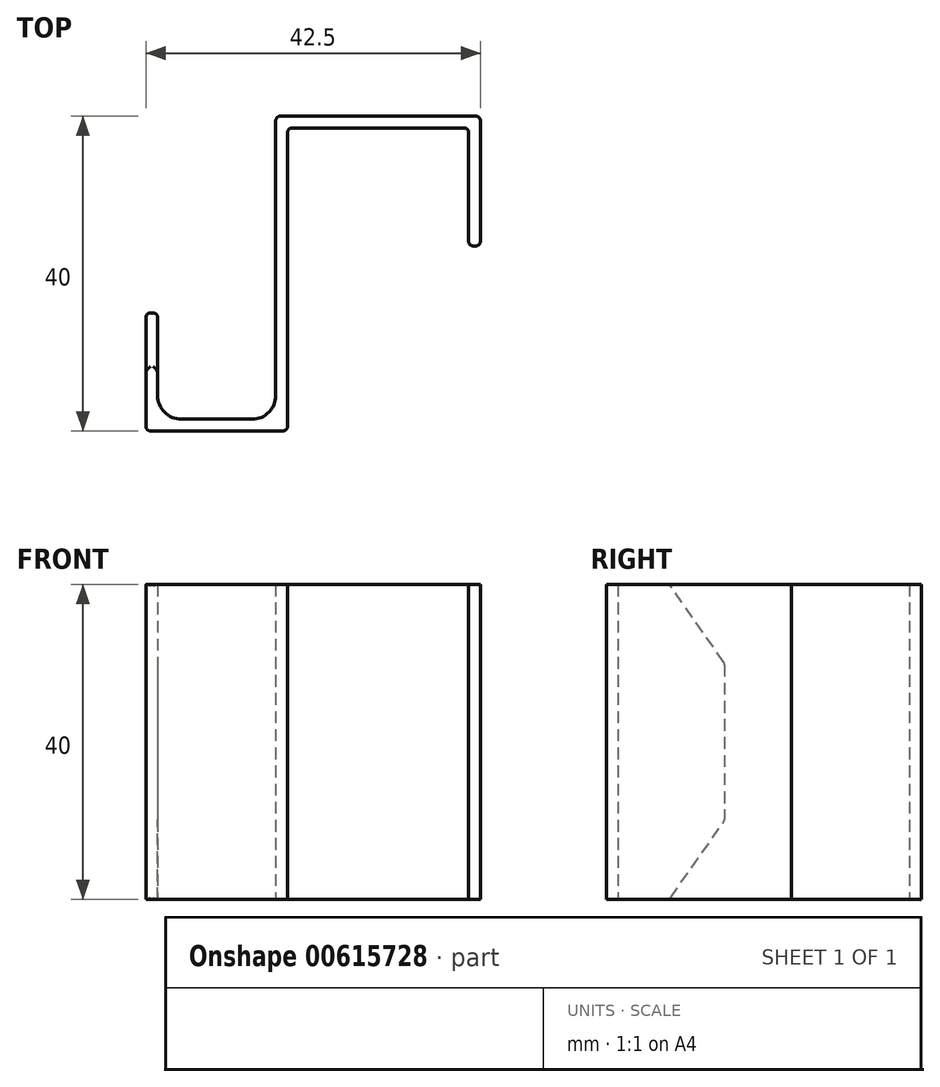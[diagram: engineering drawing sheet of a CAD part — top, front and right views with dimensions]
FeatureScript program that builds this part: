
annotation { "Feature Type Name" : "Feature", "Feature Type Description" : "" }
export const myFeature = defineFeature(function(context is Context, id is Id, definition is map)
    precondition{}
    {
        {
            var Q0;
            Q0=qCreatedBy(makeId("Top.planeOp"),FACE);
            var sketch = newSketch(context, id + "F0", { "sketchPlane" : qUnion([Q0])});
            skLineSegment(sketch, "E0.bottom", {"start": v(9.7, 5.03) * mm, "end": v(32.7, 5.03) * mm});
            skLineSegment(sketch, "E0.left", {"start": v(9.7, 5.03) * mm, "end": v(9.7, -33.47) * mm});
            skLineSegment(sketch, "E0.right", {"start": v(32.7, 5.03) * mm, "end": v(32.7, -9.97) * mm});
            skLineSegment(sketch, "E1.top", {"start": v(8.2, 6.53) * mm, "end": v(34.2, 6.53) * mm});
            skLineSegment(sketch, "E1.right", {"start": v(34.2, -9.97) * mm, "end": v(34.2, 6.53) * mm});
            skLineSegment(sketch, "E2", {"start": v(32.7, -9.97) * mm, "end": v(34.2, -9.97) * mm});
            skLineSegment(sketch, "E3", {"start": v(9.7, -33.47) * mm, "end": v(-8.3, -33.47) * mm});
            skLineSegment(sketch, "E4", {"start": v(-8.3, -33.47) * mm, "end": v(-8.3, -18.47) * mm});
            skLineSegment(sketch, "E5", {"start": v(-8.3, -18.47) * mm, "end": v(-6.8, -18.47) * mm});
            skLineSegment(sketch, "E6", {"start": v(-6.8, -18.47) * mm, "end": v(-6.8, -31.97) * mm});
            skLineSegment(sketch, "E7", {"start": v(-6.8, -31.97) * mm, "end": v(8.2, -31.97) * mm});
            skLineSegment(sketch, "E8.trimOffspring", {"start": v(8.2, -31.97) * mm, "end": v(8.2, 6.53) * mm});
            skSolve(sketch);
        }
        {
            var Q0;
            Q0 = qSketchRegion(id + "F0", true);
            extrude(context, id + "F1", {"entities" : qUnion([Q0]), "depth" : 40 * mm, "offsetDistance" : 25 * mm});
        }
        {
            var Q0;
            Q0=makeQuery(id+"F1.opExtrude","CAP_EDGE",EDGE,{"disambiguationData":[OSD([sQuery(id+"F0.wireOp",EDGE,"E5")])],"isStart":false});
            var Q1;
            Q1=makeQuery(id+"F1.opExtrude","CAP_EDGE",EDGE,{"disambiguationData":[OSD([sQuery(id+"F0.wireOp",EDGE,"E5")])],"isStart":true});
            chamfer(context, id + "F2", {"entities" : qUnion([Q0, Q1]), "chamferType" : ChamferType.OFFSET_ANGLE, "width" : 10 * mm, "oppositeDirection" : false, "angle" : 35 * degree, "tangentPropagation" : true});
        }
        {
            var Q0;
            Q0=makeQuery(id+"F1.opExtrude","SWEPT_EDGE",EDGE,{"disambiguationData":[OSD([sQuery(id+"F0.wireOp",EDGE,"E1.top"),sQuery(id+"F0.wireOp",EDGE,"E8.trimOffspring")])]});
            var Q1;
            Q1=makeQuery(id+"F1.opExtrude","SWEPT_EDGE",EDGE,{"disambiguationData":[OSD([sQuery(id+"F0.wireOp",EDGE,"E0.bottom"),sQuery(id+"F0.wireOp",EDGE,"E0.left")])]});
            var Q2;
            Q2=makeQuery(id+"F1.opExtrude","SWEPT_EDGE",EDGE,{"disambiguationData":[OSD([sQuery(id+"F0.wireOp",EDGE,"E1.right"),sQuery(id+"F0.wireOp",EDGE,"E2")])]});
            var Q3;
            Q3=makeQuery(id+"F1.opExtrude","SWEPT_EDGE",EDGE,{"disambiguationData":[OSD([sQuery(id+"F0.wireOp",EDGE,"E0.right"),sQuery(id+"F0.wireOp",EDGE,"E2")])]});
            var Q4;
            Q4=makeQuery(id+"F1.opExtrude","SWEPT_EDGE",EDGE,{"disambiguationData":[OSD([sQuery(id+"F0.wireOp",EDGE,"E0.bottom"),sQuery(id+"F0.wireOp",EDGE,"E0.right")])]});
            var Q5;
            Q5=makeQuery(id+"F1.opExtrude","SWEPT_EDGE",EDGE,{"disambiguationData":[OSD([sQuery(id+"F0.wireOp",EDGE,"E1.top"),sQuery(id+"F0.wireOp",EDGE,"E1.right")])]});
            var Q6;
            Q6=makeQuery(id+"F1.opExtrude","SWEPT_EDGE",EDGE,{"disambiguationData":[OSD([sQuery(id+"F0.wireOp",EDGE,"E5"),sQuery(id+"F0.wireOp",EDGE,"E6")])]});
            var Q7;
            Q7=makeQuery(id+"F1.opExtrude","SWEPT_EDGE",EDGE,{"disambiguationData":[OSD([sQuery(id+"F0.wireOp",EDGE,"E0.left"),sQuery(id+"F0.wireOp",EDGE,"E3")])]});
            var Q8;
            Q8=makeQuery(id+"F1.opExtrude","SWEPT_EDGE",EDGE,{"disambiguationData":[OSD([sQuery(id+"F0.wireOp",EDGE,"E4"),sQuery(id+"F0.wireOp",EDGE,"E5")])]});
            var Q9;
            Q9=makeQuery(id+"F1.opExtrude","SWEPT_EDGE",EDGE,{"disambiguationData":[OSD([sQuery(id+"F0.wireOp",EDGE,"E3"),sQuery(id+"F0.wireOp",EDGE,"E4")])]});
            var Q10;
            {var subQ0=sQuery(id+"F0.wireOp",EDGE,"E5");Q10=makeQuery(id+"F2.opChamfer","BLEND_FACE",FACE,{"disambiguationData":[OSD([subQ0]),TDD([makeQuery(id+"F1.opExtrude","CAP_EDGE",EDGE,{"disambiguationData":[OSD([subQ0])],"isStart":true})])]});}
            var Q11;
            {var subQ0=sQuery(id+"F0.wireOp",EDGE,"E5");Q11=makeQuery(id+"F2.opChamfer","BLEND_FACE",FACE,{"disambiguationData":[OSD([subQ0]),TDD([makeQuery(id+"F1.opExtrude","CAP_EDGE",EDGE,{"disambiguationData":[OSD([subQ0])],"isStart":false})])]});}
            fillet(context, id + "F3", {"entities" : qUnion([Q0, Q1, Q2, Q3, Q4, Q5, Q6, Q7, Q8, Q9, Q10, Q11]), "radius" : .6 * mm, "tangentPropagation" : true, "defaultsChanged" : false, "vertexSettings" : [], "allowEdgeOverflow" : false});
        }
        {
            var Q0;
            Q0=makeQuery(id+"F1.opExtrude","SWEPT_EDGE",EDGE,{"disambiguationData":[OSD([sQuery(id+"F0.wireOp",EDGE,"E7"),sQuery(id+"F0.wireOp",EDGE,"E8.trimOffspring")])]});
            var Q1;
            Q1=makeQuery(id+"F1.opExtrude","SWEPT_EDGE",EDGE,{"disambiguationData":[OSD([sQuery(id+"F0.wireOp",EDGE,"E6"),sQuery(id+"F0.wireOp",EDGE,"E7")])]});
            fillet(context, id + "F4", {"entities" : qUnion([Q0, Q1]), "tangentPropagation" : true, "radius" : 3 * mm, "defaultsChanged" : true, "vertexSettings" : [], "allowEdgeOverflow" : false});
        }
    });
